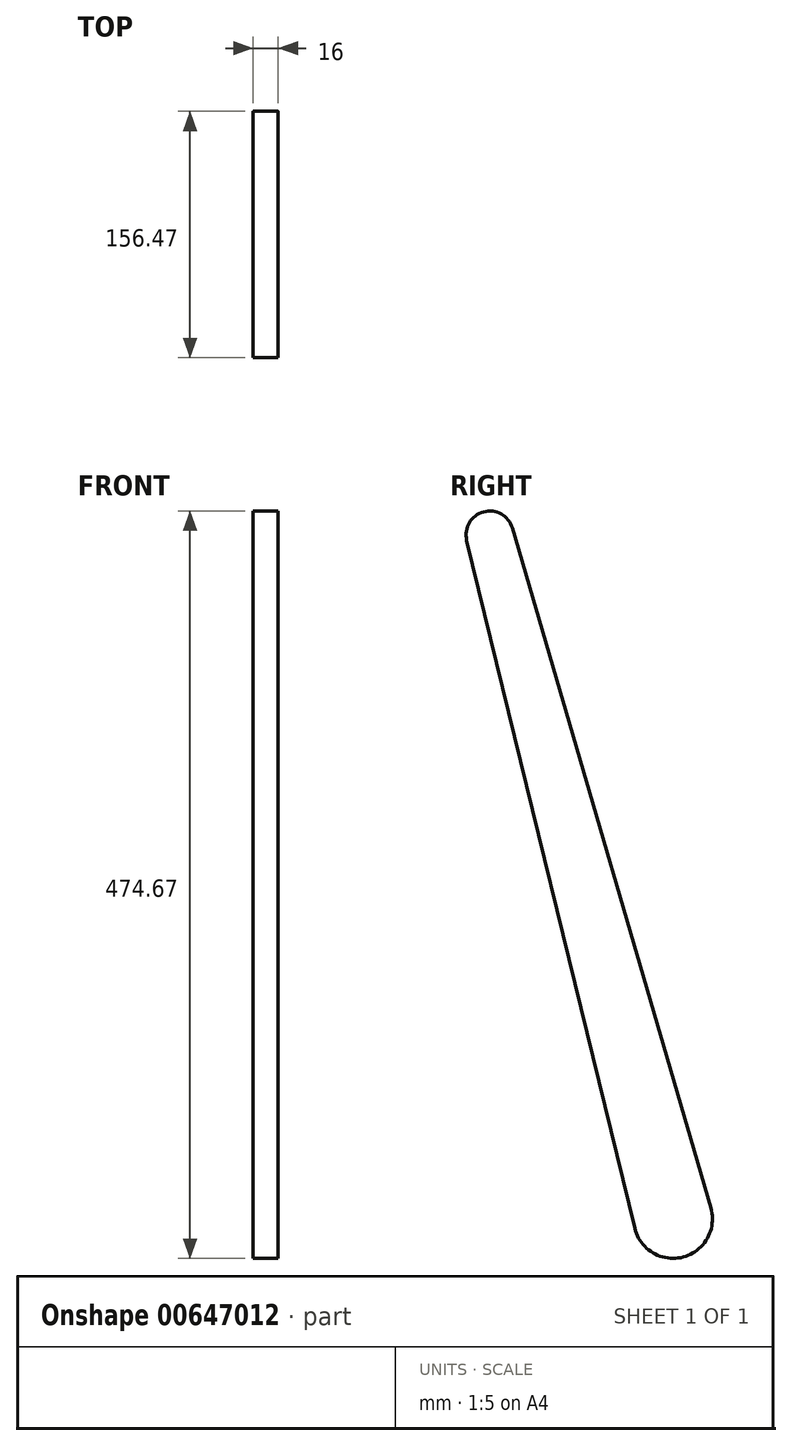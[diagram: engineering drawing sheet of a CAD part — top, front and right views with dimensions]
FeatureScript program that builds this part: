
annotation { "Feature Type Name" : "Feature", "Feature Type Description" : "" }
export const myFeature = defineFeature(function(context is Context, id is Id, definition is map)
    precondition{}
    {
        {
            var Q0;
            Q0=qCreatedBy(makeId("Right.planeOp"),FACE);
            var sketch = newSketch(context, id + "F0", { "sketchPlane" : qUnion([Q0])});
            skLineSegment(sketch, "E0", {"start": v(-102.07, 438.87) * mm, "end": v(24, 7) * mm});
            skLineSegment(sketch, "E1", {"start": v(-24.29, -5.93) * mm, "end": v(-131.04, 431.1) * mm});
            skArc(sketch, "E2.filletArc", {"start": v(-102.07, 438.87) * mm, "mid": v(-120.35, 449.16) * mm, "end": v(-131.04, 431.1) * mm});
            skLineSegment(sketch, "E3", {"start": v(-116.47, 434.67) * mm, "end": v(0, 0) * mm});
            skArc(sketch, "E4.filletArc", {"start": v(-24.29, -5.93) * mm, "mid": v(6.47, -24.15) * mm, "end": v(24, 7) * mm});
            skSolve(sketch);
        }
        {
            var Q0;
            Q0 = qSketchRegion(id + "F0", true);
            extrude(context, id + "F1", {"entities" : qUnion([Q0]), "depth" : 16 * mm, "offsetDistance" : 25 * mm});
        }
    });
